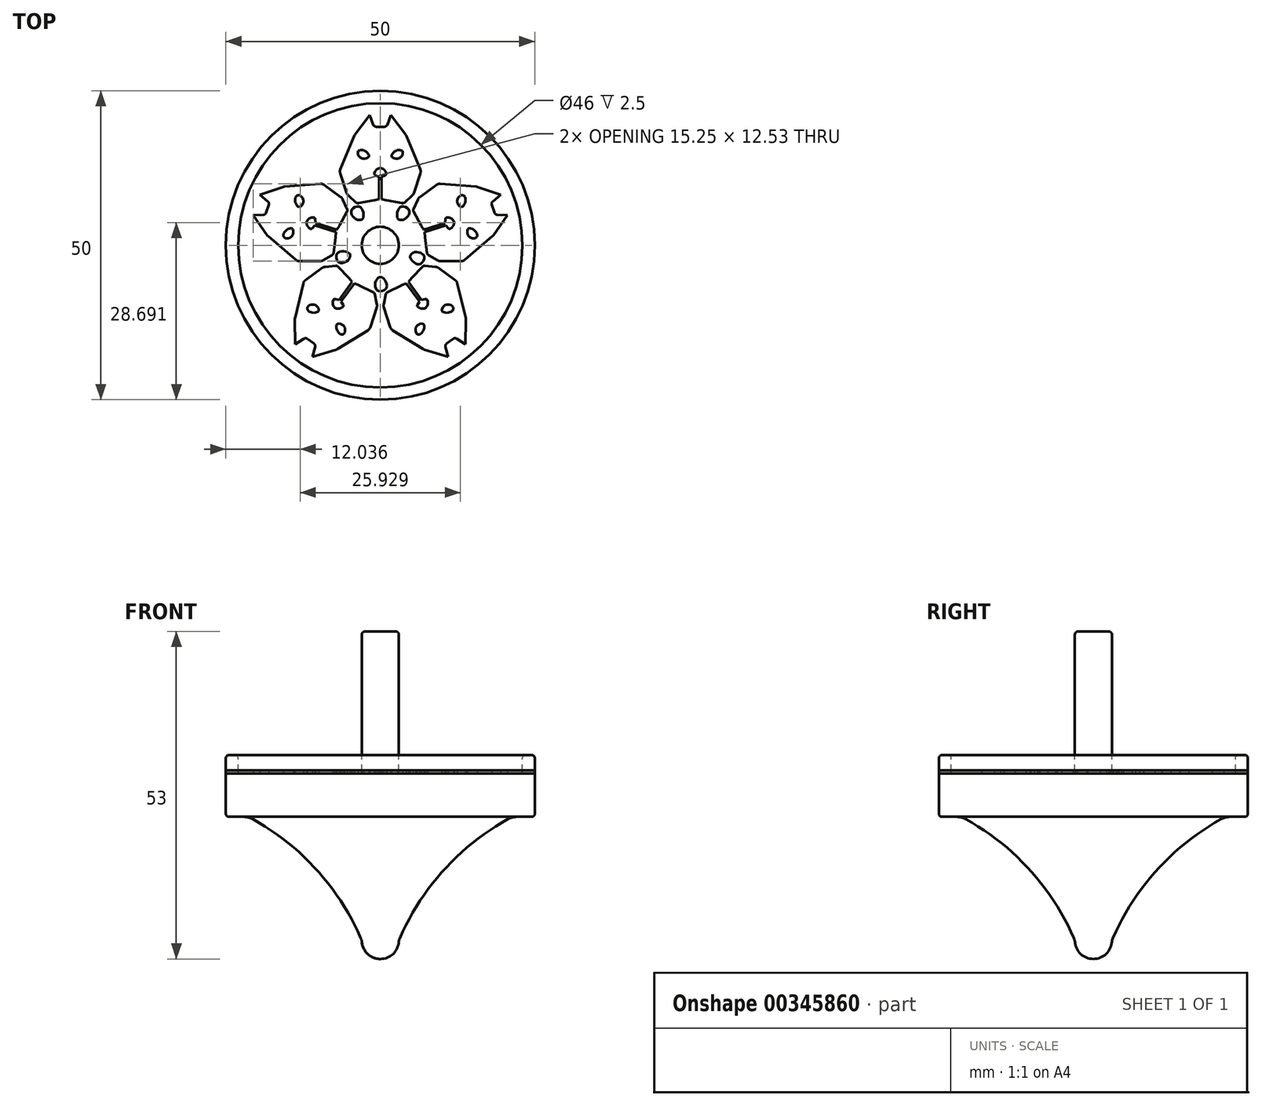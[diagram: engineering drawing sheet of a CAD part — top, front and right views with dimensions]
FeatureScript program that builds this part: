
annotation { "Feature Type Name" : "Feature", "Feature Type Description" : "" }
export const myFeature = defineFeature(function(context is Context, id is Id, definition is map)
    precondition{}
    {
        {
            var Q0;
            Q0=qCreatedBy(makeId("Front.planeOp"),FACE);
            var sketch = newSketch(context, id + "F0", { "sketchPlane" : qUnion([Q0])});
            skLineSegment(sketch, "E0", {"start": v(0, 20) * mm, "end": v(2.5, 20) * mm});
            skLineSegment(sketch, "E1.0", {"start": v(22.12, -10) * mm, "end": v(24.5, -10) * mm});
            skLineSegment(sketch, "E2.0", {"start": v(3, -3) * mm, "end": v(3, 19.5) * mm});
            skLineSegment(sketch, "E3", {"start": v(3, -30) * mm, "end": v(3, -30) * mm});
            skLineSegment(sketch, "E4", {"start": v(0, -33) * mm, "end": v(0, -33) * mm});
            skPoint(sketch, "E5.visualSharp", {"position": v(3, -33) * mm});
            skArc(sketch, "E6", {"start": v(20.66, -10.38) * mm, "mid": v(10.32, -18.56) * mm, "end": v(3.15, -29.64) * mm});
            skPoint(sketch, "E7.visualSharp", {"position": v(3, 20) * mm});
            skArc(sketch, "E7.filletArc", {"start": v(3, 19.5) * mm, "mid": v(2.85, 19.85) * mm, "end": v(2.5, 20) * mm});
            skPoint(sketch, "E8.visualSharp", {"position": v(25, 0) * mm});
            skPoint(sketch, "E9.visualSharp", {"position": v(25, -10) * mm});
            skArc(sketch, "E9.filletArc", {"start": v(24.5, -10) * mm, "mid": v(24.85, -9.85) * mm, "end": v(25, -9.5) * mm});
            skArc(sketch, "E10.filletArc", {"start": v(22.12, -10) * mm, "mid": v(21.37, -10.1) * mm, "end": v(20.66, -10.38) * mm});
            skPoint(sketch, "E11.orphan", {"position": v(0, 0) * mm});
            skPoint(sketch, "E12.visualSharp", {"position": v(3, -30) * mm});
            skArc(sketch, "E13.filletArc", {"start": v(0, -33) * mm, "mid": v(2.06, -32.18) * mm, "end": v(3, -30.16) * mm});
            skLineSegment(sketch, "E14", {"start": v(3.08, -29.83) * mm, "end": v(3.15, -29.64) * mm});
            skArc(sketch, "E15.filletArc", {"start": v(3.08, -29.83) * mm, "mid": v(3.02, -30) * mm, "end": v(3, -30.16) * mm});
            skLineSegment(sketch, "E16", {"start": v(0, 20) * mm, "end": v(0, -33) * mm});
            skLineSegment(sketch, "E17.0", {"start": v(3, -3) * mm, "end": v(23, -3) * mm});
            skPoint(sketch, "E18.visualSharp", {"position": v(23, 0) * mm});
            skPoint(sketch, "E19.orphan", {"position": v(23, -10) * mm});
            skLineSegment(sketch, "E20", {"start": v(23, -3) * mm, "end": v(25, -3) * mm});
            skLineSegment(sketch, "E21", {"start": v(25, -3) * mm, "end": v(25, -9.5) * mm});
            skSolve(sketch);
        }
        {
            var Q0;
            Q0 = qSketchRegion(id + "F0", true);
            var Q1;
            Q1=sQuery(id+"F0.wireOp",EDGE,"E16");
            revolve(context, id + "F1", {"entities" : qUnion([Q0]), "axis" : qUnion([Q1]), "revolveType" : RevolveType.FULL});
        }
        {
            var Q0;
            Q0=qCreatedBy(makeId("Front.planeOp"),FACE);
            var sketch = newSketch(context, id + "F2", { "sketchPlane" : qUnion([Q0])});
            skLineSegment(sketch, "E22", {"start": v(0, 17.36) * mm, "end": v(0, 0) * mm});
            skLineSegment(sketch, "E23", {"start": v(23.5, 0) * mm, "end": v(24.5, 0) * mm});
            skLineSegment(sketch, "E24", {"start": v(23, -0.5) * mm, "end": v(23, -3) * mm});
            skLineSegment(sketch, "E25.0", {"start": v(25, -0.5) * mm, "end": v(25, -3) * mm});
            skPoint(sketch, "E26.visualSharp", {"position": v(23, 0) * mm});
            skArc(sketch, "E26.filletArc", {"start": v(23.5, 0) * mm, "mid": v(23.15, -0.15) * mm, "end": v(23, -0.5) * mm});
            skPoint(sketch, "E27.visualSharp", {"position": v(25, 0) * mm});
            skArc(sketch, "E27.filletArc", {"start": v(25, -0.5) * mm, "mid": v(24.85, -0.15) * mm, "end": v(24.5, 0) * mm});
            skLineSegment(sketch, "E28", {"start": v(23, -3) * mm, "end": v(25, -3) * mm});
            skSolve(sketch);
        }
        {
            var Q0;
            Q0=makeQuery(id+"F2.imprint","IMPRINT",FACE,{"disambiguationData":[TD([[makeQuery(id+"F2.imprint","IMPRINT",EDGE,{"derivedFrom":sQuery(id+"F2.wireOp",EDGE,"E23")}),-1.0]])]});
            var Q1;
            Q1=sQuery(id+"F2.wireOp",EDGE,"E22");
            revolve(context, id + "F3", {"entities" : qUnion([Q0]), "axis" : qUnion([Q1]), "revolveType" : RevolveType.FULL});
        }
        {
            var Q0;
            Q0=makeQuery(id+"F1.opRevolve","SWEPT_FACE",FACE,{"disambiguationData":[OSD([sQuery(id+"F0.wireOp",EDGE,"E17.0"),sQuery(id+"F0.wireOp",EDGE,"E20")])]});
            var sketch = newSketch(context, id + "F4", { "sketchPlane" : qUnion([Q0])});
            skLineSegment(sketch, "E29", {"start": v(0.2, 7.45) * mm, "end": v(0.97, 7.28) * mm});
            skLineSegment(sketch, "E30", {"start": v(1.02, 7.27) * mm, "end": v(3.5, 6.81) * mm});
            skLineSegment(sketch, "E31", {"start": v(3.92, 6.93) * mm, "end": v(5.17, 8.06) * mm});
            skLineSegment(sketch, "E32", {"start": v(5.45, 8.5) * mm, "end": v(6.48, 11.63) * mm});
            skLineSegment(sketch, "E33", {"start": v(6.46, 12.33) * mm, "end": v(4.25, 17.65) * mm});
            skLineSegment(sketch, "E34", {"start": v(4.13, 17.86) * mm, "end": v(1.75, 21.08) * mm});
            skLineSegment(sketch, "E35", {"start": v(1.75, 21.08) * mm, "end": v(1.13, 19.5) * mm});
            skLineSegment(sketch, "E36", {"start": v(0.67, 19.19) * mm, "end": v(0, 19.19) * mm});
            skPoint(sketch, "E37.visualSharp", {"position": v(1, 7.27) * mm});
            skArc(sketch, "E37.filletArc", {"start": v(0.97, 7.28) * mm, "mid": v(1, 7.27) * mm, "end": v(1.02, 7.27) * mm});
            skPoint(sketch, "E38.visualSharp", {"position": v(3.74, 6.77) * mm});
            skArc(sketch, "E38.filletArc", {"start": v(3.5, 6.81) * mm, "mid": v(3.72, 6.82) * mm, "end": v(3.92, 6.93) * mm});
            skPoint(sketch, "E39.visualSharp", {"position": v(5.37, 8.24) * mm});
            skArc(sketch, "E39.filletArc", {"start": v(5.17, 8.06) * mm, "mid": v(5.34, 8.26) * mm, "end": v(5.45, 8.5) * mm});
            skPoint(sketch, "E40.visualSharp", {"position": v(6.6, 11.99) * mm});
            skArc(sketch, "E40.filletArc", {"start": v(6.48, 11.63) * mm, "mid": v(6.53, 11.98) * mm, "end": v(6.46, 12.33) * mm});
            skPoint(sketch, "E41.visualSharp", {"position": v(4.2, 17.76) * mm});
            skArc(sketch, "E41.filletArc", {"start": v(4.25, 17.65) * mm, "mid": v(4.2, 17.76) * mm, "end": v(4.13, 17.86) * mm});
            skPoint(sketch, "E42.visualSharp", {"position": v(1, 19.19) * mm});
            skArc(sketch, "E42.filletArc", {"start": v(0.67, 19.19) * mm, "mid": v(0.95, 19.27) * mm, "end": v(1.13, 19.5) * mm});
            skLineSegment(sketch, "E43", {"start": v(0.2, 11.08) * mm, "end": v(0.76, 11.3) * mm});
            skLineSegment(sketch, "E44", {"start": v(0.93, 11.7) * mm, "end": v(0.86, 11.88) * mm});
            skLineSegment(sketch, "E45", {"start": v(0.24, 12.46) * mm, "end": v(0, 12.54) * mm});
            skFitSpline(sketch, "E46", {"points": [v(1.85, 14.44) * mm, v(2.8, 15.4) * mm, v(3.63, 15.1) * mm, v(2.98, 14.05) * mm, v(1.85, 14.44) * mm]});
            skPoint(sketch, "E47.1.internal.snap0", {"position": v(0.49, 7.39) * mm});
            skPoint(sketch, "E48.visualSharp", {"position": v(0.68, 12.31) * mm});
            skArc(sketch, "E48.filletArc", {"start": v(0.86, 11.88) * mm, "mid": v(0.61, 12.24) * mm, "end": v(0.24, 12.46) * mm});
            skPoint(sketch, "E49.visualSharp", {"position": v(1.04, 11.41) * mm});
            skArc(sketch, "E49.filletArc", {"start": v(0.76, 11.3) * mm, "mid": v(0.93, 11.46) * mm, "end": v(0.93, 11.7) * mm});
            skLineSegment(sketch, "E50.MirrorCS", {"start": v(-0.67, 19.19) * mm, "end": v(0, 19.19) * mm});
            skPoint(sketch, "E51.MirrorP", {"position": v(-1, 19.19) * mm});
            skArc(sketch, "E52.MirrorCS", {"start": v(-0.67, 19.19) * mm, "mid": v(-0.95, 19.27) * mm, "end": v(-1.13, 19.5) * mm});
            skLineSegment(sketch, "E53.MirrorCS", {"start": v(-1.75, 21.08) * mm, "end": v(-1.13, 19.5) * mm});
            skLineSegment(sketch, "E54.MirrorCS", {"start": v(-4.13, 17.86) * mm, "end": v(-1.75, 21.08) * mm});
            skArc(sketch, "E55.MirrorCS", {"start": v(-4.25, 17.65) * mm, "mid": v(-4.2, 17.76) * mm, "end": v(-4.13, 17.86) * mm});
            skLineSegment(sketch, "E56.MirrorCS", {"start": v(-6.46, 12.33) * mm, "end": v(-4.25, 17.65) * mm});
            skArc(sketch, "E57.MirrorCS", {"start": v(-6.48, 11.63) * mm, "mid": v(-6.53, 11.98) * mm, "end": v(-6.46, 12.33) * mm});
            skLineSegment(sketch, "E58.MirrorCS", {"start": v(-5.45, 8.5) * mm, "end": v(-6.48, 11.63) * mm});
            skArc(sketch, "E59.MirrorCS", {"start": v(-5.17, 8.06) * mm, "mid": v(-5.34, 8.26) * mm, "end": v(-5.45, 8.5) * mm});
            skLineSegment(sketch, "E60.MirrorCS", {"start": v(-3.92, 6.93) * mm, "end": v(-5.17, 8.06) * mm});
            skArc(sketch, "E61.MirrorCS", {"start": v(-3.5, 6.81) * mm, "mid": v(-3.72, 6.82) * mm, "end": v(-3.92, 6.93) * mm});
            skLineSegment(sketch, "E62.MirrorCS", {"start": v(-1.02, 7.27) * mm, "end": v(-3.5, 6.81) * mm});
            skLineSegment(sketch, "E63.MirrorCS", {"start": v(-0.2, 7.45) * mm, "end": v(-0.97, 7.28) * mm});
            skLineSegment(sketch, "E64.MirrorCS", {"start": v(-0.24, 12.46) * mm, "end": v(0, 12.54) * mm});
            skArc(sketch, "E65.MirrorCS", {"start": v(-0.86, 11.88) * mm, "mid": v(-0.61, 12.24) * mm, "end": v(-0.24, 12.46) * mm});
            skLineSegment(sketch, "E66.MirrorCS", {"start": v(-0.93, 11.7) * mm, "end": v(-0.86, 11.88) * mm});
            skArc(sketch, "E67.MirrorCS", {"start": v(-0.76, 11.3) * mm, "mid": v(-0.93, 11.46) * mm, "end": v(-0.93, 11.7) * mm});
            skLineSegment(sketch, "E68.MirrorCS", {"start": v(-0.2, 11.08) * mm, "end": v(-0.76, 11.3) * mm});
            skFitSpline(sketch, "E69.MirrorC", {"points": [v(-1.85, 14.44) * mm, v(-2.8, 15.4) * mm, v(-3.63, 15.1) * mm, v(-2.98, 14.05) * mm, v(-1.85, 14.44) * mm]});
            skFitSpline(sketch, "E70", {"points": [v(2.97, 4.18) * mm, v(2.7, 4.91) * mm, v(3.34, 6.21) * mm, v(4.7, 5.63) * mm, v(3.98, 4.26) * mm, v(2.97, 4.18) * mm]});
            skPoint(sketch, "E71.MirrorP", {"position": v(-4.2, 17.76) * mm});
            skPoint(sketch, "E72.MirrorP", {"position": v(-6.6, 11.99) * mm});
            skPoint(sketch, "E73.MirrorP", {"position": v(-5.37, 8.24) * mm});
            skPoint(sketch, "E74.MirrorP", {"position": v(-3.74, 6.77) * mm});
            skPoint(sketch, "E75.MirrorP", {"position": v(-0.49, 7.39) * mm});
            skPoint(sketch, "E76.MirrorP", {"position": v(-1, 7.27) * mm});
            skPoint(sketch, "E77.MirrorP", {"position": v(-0.68, 12.31) * mm});
            skPoint(sketch, "E78.MirrorP", {"position": v(-1.04, 11.41) * mm});
            skArc(sketch, "E79.MirrorCS", {"start": v(-0.97, 7.28) * mm, "mid": v(-1, 7.27) * mm, "end": v(-1.02, 7.27) * mm});
            skLineSegment(sketch, "E80.0", {"start": v(-0.2, 11.08) * mm, "end": v(-0.2, 7.45) * mm});
            skLineSegment(sketch, "E81.0", {"start": v(0.2, 11.08) * mm, "end": v(0.2, 7.45) * mm});
            skLineSegment(sketch, "E82", {"start": v(0, 7.5) * mm, "end": v(0, 0) * mm});
            skLineSegment(sketch, "E83.1.0", {"start": v(-18.26, 1.6) * mm, "end": v(-20.59, 4.85) * mm});
            skLineSegment(sketch, "E83.1.1", {"start": v(-20.59, 4.85) * mm, "end": v(-18.9, 4.95) * mm});
            skArc(sketch, "E83.1.2", {"start": v(-18.45, 5.3) * mm, "mid": v(-18.62, 5.05) * mm, "end": v(-18.9, 4.95) * mm});
            skLineSegment(sketch, "E83.1.3", {"start": v(-18.45, 5.3) * mm, "end": v(-18.25, 5.93) * mm});
            skLineSegment(sketch, "E83.1.4", {"start": v(-18.04, 6.56) * mm, "end": v(-18.25, 5.93) * mm});
            skArc(sketch, "E83.1.5", {"start": v(-18.04, 6.56) * mm, "mid": v(-18.04, 6.86) * mm, "end": v(-18.2, 7.1) * mm});
            skLineSegment(sketch, "E83.1.6", {"start": v(-19.5, 8.17) * mm, "end": v(-18.2, 7.1) * mm});
            skLineSegment(sketch, "E83.1.7", {"start": v(-15.71, 9.45) * mm, "end": v(-19.5, 8.17) * mm});
            skArc(sketch, "E83.1.8", {"start": v(-15.47, 9.5) * mm, "mid": v(-15.6, 9.48) * mm, "end": v(-15.71, 9.45) * mm});
            skLineSegment(sketch, "E83.1.9", {"start": v(-9.73, 9.95) * mm, "end": v(-15.47, 9.5) * mm});
            skArc(sketch, "E83.1.10", {"start": v(-9.06, 9.76) * mm, "mid": v(-9.38, 9.92) * mm, "end": v(-9.73, 9.95) * mm});
            skLineSegment(sketch, "E83.1.11", {"start": v(-6.39, 7.81) * mm, "end": v(-9.06, 9.76) * mm});
            skArc(sketch, "E83.1.12", {"start": v(-6.07, 7.4) * mm, "mid": v(-6.2, 7.63) * mm, "end": v(-6.39, 7.81) * mm});
            skLineSegment(sketch, "E83.1.13", {"start": v(-5.38, 5.87) * mm, "end": v(-6.07, 7.4) * mm});
            skArc(sketch, "E83.1.14", {"start": v(-5.4, 5.43) * mm, "mid": v(-5.34, 5.65) * mm, "end": v(-5.38, 5.87) * mm});
            skLineSegment(sketch, "E83.1.15", {"start": v(-6.6, 3.21) * mm, "end": v(-5.4, 5.43) * mm});
            skLineSegment(sketch, "E83.1.16", {"start": v(-7.03, 2.5) * mm, "end": v(-6.62, 3.17) * mm});
            skLineSegment(sketch, "E83.1.17", {"start": v(-7.15, 2.11) * mm, "end": v(-7.22, 1.32) * mm});
            skLineSegment(sketch, "E83.1.18", {"start": v(-7.23, 1.28) * mm, "end": v(-7.56, -1.22) * mm});
            skArc(sketch, "E83.1.19", {"start": v(-7.56, -1.22) * mm, "mid": v(-7.64, -1.43) * mm, "end": v(-7.8, -1.58) * mm});
            skLineSegment(sketch, "E83.1.20", {"start": v(-7.8, -1.58) * mm, "end": v(-9.26, -2.43) * mm});
            skArc(sketch, "E83.1.21", {"start": v(-9.26, -2.43) * mm, "mid": v(-9.5, -2.53) * mm, "end": v(-9.76, -2.56) * mm});
            skLineSegment(sketch, "E83.1.22", {"start": v(-9.76, -2.56) * mm, "end": v(-13.07, -2.57) * mm});
            skArc(sketch, "E83.1.23", {"start": v(-13.07, -2.57) * mm, "mid": v(-13.42, -2.51) * mm, "end": v(-13.72, -2.33) * mm});
            skLineSegment(sketch, "E83.1.24", {"start": v(-13.72, -2.33) * mm, "end": v(-18.1, 1.41) * mm});
            skArc(sketch, "E83.1.25", {"start": v(-18.1, 1.41) * mm, "mid": v(-18.19, 1.5) * mm, "end": v(-18.26, 1.6) * mm});
            skLineSegment(sketch, "E83.2.0", {"start": v(-7.16, -16.88) * mm, "end": v(-10.98, -18.08) * mm});
            skLineSegment(sketch, "E83.2.1", {"start": v(-10.98, -18.08) * mm, "end": v(-10.55, -16.45) * mm});
            skArc(sketch, "E83.2.2", {"start": v(-10.74, -15.91) * mm, "mid": v(-10.56, -16.15) * mm, "end": v(-10.55, -16.45) * mm});
            skLineSegment(sketch, "E83.2.3", {"start": v(-10.74, -15.91) * mm, "end": v(-11.28, -15.52) * mm});
            skLineSegment(sketch, "E83.2.4", {"start": v(-11.82, -15.13) * mm, "end": v(-11.28, -15.52) * mm});
            skArc(sketch, "E83.2.5", {"start": v(-11.82, -15.13) * mm, "mid": v(-12.1, -15.04) * mm, "end": v(-12.38, -15.11) * mm});
            skLineSegment(sketch, "E83.2.6", {"start": v(-13.8, -16.03) * mm, "end": v(-12.38, -15.11) * mm});
            skLineSegment(sketch, "E83.2.7", {"start": v(-13.84, -12.02) * mm, "end": v(-13.8, -16.03) * mm});
            skArc(sketch, "E83.2.8", {"start": v(-13.81, -11.78) * mm, "mid": v(-13.83, -11.9) * mm, "end": v(-13.84, -12.02) * mm});
            skLineSegment(sketch, "E83.2.9", {"start": v(-12.47, -6.18) * mm, "end": v(-13.81, -11.78) * mm});
            skArc(sketch, "E83.2.10", {"start": v(-12.08, -5.6) * mm, "mid": v(-12.33, -5.85) * mm, "end": v(-12.47, -6.18) * mm});
            skLineSegment(sketch, "E83.2.11", {"start": v(-9.4, -3.66) * mm, "end": v(-12.08, -5.6) * mm});
            skArc(sketch, "E83.2.12", {"start": v(-8.92, -3.48) * mm, "mid": v(-9.17, -3.54) * mm, "end": v(-9.4, -3.66) * mm});
            skLineSegment(sketch, "E83.2.13", {"start": v(-7.25, -3.3) * mm, "end": v(-8.92, -3.48) * mm});
            skArc(sketch, "E83.2.14", {"start": v(-6.83, -3.46) * mm, "mid": v(-7.02, -3.33) * mm, "end": v(-7.25, -3.3) * mm});
            skLineSegment(sketch, "E83.2.15", {"start": v(-5.1, -5.28) * mm, "end": v(-6.83, -3.46) * mm});
            skLineSegment(sketch, "E83.2.16", {"start": v(-4.54, -5.91) * mm, "end": v(-5.06, -5.31) * mm});
            skLineSegment(sketch, "E83.2.17", {"start": v(-4.22, -6.15) * mm, "end": v(-3.49, -6.46) * mm});
            skLineSegment(sketch, "E83.2.18", {"start": v(-3.45, -6.48) * mm, "end": v(-1.18, -7.57) * mm});
            skArc(sketch, "E83.2.19", {"start": v(-1.18, -7.57) * mm, "mid": v(-1, -7.7) * mm, "end": v(-0.9, -7.91) * mm});
            skLineSegment(sketch, "E83.2.20", {"start": v(-0.9, -7.91) * mm, "end": v(-0.55, -9.56) * mm});
            skArc(sketch, "E83.2.21", {"start": v(-0.55, -9.56) * mm, "mid": v(-0.53, -9.82) * mm, "end": v(-0.58, -10.08) * mm});
            skLineSegment(sketch, "E83.2.22", {"start": v(-0.58, -10.08) * mm, "end": v(-1.6, -13.22) * mm});
            skArc(sketch, "E83.2.23", {"start": v(-1.6, -13.22) * mm, "mid": v(-1.76, -13.53) * mm, "end": v(-2.02, -13.77) * mm});
            skLineSegment(sketch, "E83.2.24", {"start": v(-2.02, -13.77) * mm, "end": v(-6.94, -16.78) * mm});
            skArc(sketch, "E83.2.25", {"start": v(-6.94, -16.78) * mm, "mid": v(-7.04, -16.83) * mm, "end": v(-7.16, -16.88) * mm});
            skLineSegment(sketch, "E83.3.0", {"start": v(13.84, -12.02) * mm, "end": v(13.8, -16.03) * mm});
            skLineSegment(sketch, "E83.3.1", {"start": v(13.8, -16.03) * mm, "end": v(12.38, -15.11) * mm});
            skArc(sketch, "E83.3.2", {"start": v(11.82, -15.13) * mm, "mid": v(12.1, -15.04) * mm, "end": v(12.38, -15.11) * mm});
            skLineSegment(sketch, "E83.3.3", {"start": v(11.82, -15.13) * mm, "end": v(11.28, -15.52) * mm});
            skLineSegment(sketch, "E83.3.4", {"start": v(10.74, -15.91) * mm, "end": v(11.28, -15.52) * mm});
            skArc(sketch, "E83.3.5", {"start": v(10.74, -15.91) * mm, "mid": v(10.56, -16.15) * mm, "end": v(10.55, -16.45) * mm});
            skLineSegment(sketch, "E83.3.6", {"start": v(10.98, -18.08) * mm, "end": v(10.55, -16.45) * mm});
            skLineSegment(sketch, "E83.3.7", {"start": v(7.16, -16.88) * mm, "end": v(10.98, -18.08) * mm});
            skArc(sketch, "E83.3.8", {"start": v(6.94, -16.78) * mm, "mid": v(7.04, -16.83) * mm, "end": v(7.16, -16.88) * mm});
            skLineSegment(sketch, "E83.3.9", {"start": v(2.02, -13.77) * mm, "end": v(6.94, -16.78) * mm});
            skArc(sketch, "E83.3.10", {"start": v(1.6, -13.22) * mm, "mid": v(1.76, -13.53) * mm, "end": v(2.02, -13.77) * mm});
            skLineSegment(sketch, "E83.3.11", {"start": v(0.58, -10.08) * mm, "end": v(1.6, -13.22) * mm});
            skArc(sketch, "E83.3.12", {"start": v(0.55, -9.56) * mm, "mid": v(0.53, -9.82) * mm, "end": v(0.58, -10.08) * mm});
            skLineSegment(sketch, "E83.3.13", {"start": v(0.9, -7.91) * mm, "end": v(0.55, -9.56) * mm});
            skArc(sketch, "E83.3.14", {"start": v(1.18, -7.57) * mm, "mid": v(1, -7.7) * mm, "end": v(0.9, -7.91) * mm});
            skLineSegment(sketch, "E83.3.15", {"start": v(3.45, -6.48) * mm, "end": v(1.18, -7.57) * mm});
            skLineSegment(sketch, "E83.3.16", {"start": v(4.22, -6.15) * mm, "end": v(3.49, -6.46) * mm});
            skLineSegment(sketch, "E83.3.17", {"start": v(4.54, -5.91) * mm, "end": v(5.06, -5.31) * mm});
            skLineSegment(sketch, "E83.3.18", {"start": v(5.1, -5.28) * mm, "end": v(6.83, -3.46) * mm});
            skArc(sketch, "E83.3.19", {"start": v(6.83, -3.46) * mm, "mid": v(7.02, -3.33) * mm, "end": v(7.25, -3.3) * mm});
            skLineSegment(sketch, "E83.3.20", {"start": v(7.25, -3.3) * mm, "end": v(8.92, -3.48) * mm});
            skArc(sketch, "E83.3.21", {"start": v(8.92, -3.48) * mm, "mid": v(9.17, -3.54) * mm, "end": v(9.4, -3.66) * mm});
            skLineSegment(sketch, "E83.3.22", {"start": v(9.4, -3.66) * mm, "end": v(12.08, -5.6) * mm});
            skArc(sketch, "E83.3.23", {"start": v(12.08, -5.6) * mm, "mid": v(12.33, -5.85) * mm, "end": v(12.47, -6.18) * mm});
            skLineSegment(sketch, "E83.3.24", {"start": v(12.47, -6.18) * mm, "end": v(13.81, -11.78) * mm});
            skArc(sketch, "E83.3.25", {"start": v(13.81, -11.78) * mm, "mid": v(13.83, -11.9) * mm, "end": v(13.84, -12.02) * mm});
            skLineSegment(sketch, "E83.4.0", {"start": v(15.71, 9.45) * mm, "end": v(19.5, 8.17) * mm});
            skLineSegment(sketch, "E83.4.1", {"start": v(19.5, 8.17) * mm, "end": v(18.2, 7.1) * mm});
            skArc(sketch, "E83.4.2", {"start": v(18.04, 6.56) * mm, "mid": v(18.04, 6.86) * mm, "end": v(18.2, 7.1) * mm});
            skLineSegment(sketch, "E83.4.3", {"start": v(18.04, 6.56) * mm, "end": v(18.25, 5.93) * mm});
            skLineSegment(sketch, "E83.4.4", {"start": v(18.45, 5.3) * mm, "end": v(18.25, 5.93) * mm});
            skArc(sketch, "E83.4.5", {"start": v(18.45, 5.3) * mm, "mid": v(18.62, 5.05) * mm, "end": v(18.9, 4.95) * mm});
            skLineSegment(sketch, "E83.4.6", {"start": v(20.59, 4.85) * mm, "end": v(18.9, 4.95) * mm});
            skLineSegment(sketch, "E83.4.7", {"start": v(18.26, 1.6) * mm, "end": v(20.59, 4.85) * mm});
            skArc(sketch, "E83.4.8", {"start": v(18.1, 1.41) * mm, "mid": v(18.19, 1.5) * mm, "end": v(18.26, 1.6) * mm});
            skLineSegment(sketch, "E83.4.9", {"start": v(13.72, -2.33) * mm, "end": v(18.1, 1.41) * mm});
            skArc(sketch, "E83.4.10", {"start": v(13.07, -2.57) * mm, "mid": v(13.42, -2.51) * mm, "end": v(13.72, -2.33) * mm});
            skLineSegment(sketch, "E83.4.11", {"start": v(9.76, -2.56) * mm, "end": v(13.07, -2.57) * mm});
            skArc(sketch, "E83.4.12", {"start": v(9.26, -2.43) * mm, "mid": v(9.5, -2.53) * mm, "end": v(9.76, -2.56) * mm});
            skLineSegment(sketch, "E83.4.13", {"start": v(7.8, -1.58) * mm, "end": v(9.26, -2.43) * mm});
            skArc(sketch, "E83.4.14", {"start": v(7.56, -1.22) * mm, "mid": v(7.64, -1.43) * mm, "end": v(7.8, -1.58) * mm});
            skLineSegment(sketch, "E83.4.15", {"start": v(7.23, 1.28) * mm, "end": v(7.56, -1.22) * mm});
            skLineSegment(sketch, "E83.4.16", {"start": v(7.15, 2.11) * mm, "end": v(7.22, 1.32) * mm});
            skLineSegment(sketch, "E83.4.17", {"start": v(7.03, 2.5) * mm, "end": v(6.62, 3.17) * mm});
            skLineSegment(sketch, "E83.4.18", {"start": v(6.6, 3.21) * mm, "end": v(5.4, 5.43) * mm});
            skArc(sketch, "E83.4.19", {"start": v(5.4, 5.43) * mm, "mid": v(5.34, 5.65) * mm, "end": v(5.38, 5.87) * mm});
            skLineSegment(sketch, "E83.4.20", {"start": v(5.38, 5.87) * mm, "end": v(6.07, 7.4) * mm});
            skArc(sketch, "E83.4.21", {"start": v(6.07, 7.4) * mm, "mid": v(6.2, 7.63) * mm, "end": v(6.39, 7.81) * mm});
            skLineSegment(sketch, "E83.4.22", {"start": v(6.39, 7.81) * mm, "end": v(9.06, 9.76) * mm});
            skArc(sketch, "E83.4.23", {"start": v(9.06, 9.76) * mm, "mid": v(9.38, 9.92) * mm, "end": v(9.73, 9.95) * mm});
            skLineSegment(sketch, "E83.4.24", {"start": v(9.73, 9.95) * mm, "end": v(15.47, 9.5) * mm});
            skArc(sketch, "E83.4.25", {"start": v(15.47, 9.5) * mm, "mid": v(15.6, 9.48) * mm, "end": v(15.71, 9.45) * mm});
            skPoint(sketch, "E83.center", {"position": v(0, 0) * mm});
            skArc(sketch, "E84.1.0", {"start": v(-5.81, -4.48) * mm, "mid": v(-5.8, -4.5) * mm, "end": v(-5.78, -4.51) * mm});
            skArc(sketch, "E84.2.0", {"start": v(6.79, -2.8) * mm, "mid": v(6.8, -2.77) * mm, "end": v(6.8, -2.75) * mm});
            skArc(sketch, "E85.1.0", {"start": v(-7.22, 1.32) * mm, "mid": v(-7.22, 1.3) * mm, "end": v(-7.23, 1.28) * mm});
            skArc(sketch, "E85.2.0", {"start": v(-3.49, -6.46) * mm, "mid": v(-3.47, -6.47) * mm, "end": v(-3.45, -6.48) * mm});
            skArc(sketch, "E85.3.0", {"start": v(5.06, -5.31) * mm, "mid": v(5.08, -5.3) * mm, "end": v(5.1, -5.28) * mm});
            skArc(sketch, "E85.4.0", {"start": v(6.62, 3.17) * mm, "mid": v(6.6, 3.2) * mm, "end": v(6.6, 3.21) * mm});
            skArc(sketch, "E86.1.0", {"start": v(-6.62, 3.17) * mm, "mid": v(-6.6, 3.2) * mm, "end": v(-6.6, 3.21) * mm});
            skArc(sketch, "E86.2.0", {"start": v(-5.06, -5.31) * mm, "mid": v(-5.08, -5.3) * mm, "end": v(-5.1, -5.28) * mm});
            skArc(sketch, "E86.3.0", {"start": v(3.49, -6.46) * mm, "mid": v(3.47, -6.47) * mm, "end": v(3.45, -6.48) * mm});
            skArc(sketch, "E86.4.0", {"start": v(7.22, 1.32) * mm, "mid": v(7.22, 1.3) * mm, "end": v(7.23, 1.28) * mm});
            skPoint(sketch, "E87.orphan", {"position": v(0, 7.5) * mm});
            skPoint(sketch, "E88.orphan", {"position": v(0, 11) * mm});
            skArc(sketch, "E89.1.0", {"start": v(-11.56, 2.86) * mm, "mid": v(-11.83, 3.2) * mm, "end": v(-11.92, 3.62) * mm});
            skLineSegment(sketch, "E89.1.1", {"start": v(-11.92, 3.62) * mm, "end": v(-11.92, 3.87) * mm});
            skLineSegment(sketch, "E89.1.2", {"start": v(-11.78, 4.08) * mm, "end": v(-11.92, 3.87) * mm});
            skArc(sketch, "E89.1.3", {"start": v(-11.03, 4.49) * mm, "mid": v(-11.45, 4.36) * mm, "end": v(-11.78, 4.08) * mm});
            skLineSegment(sketch, "E89.1.4", {"start": v(-10.83, 4.5) * mm, "end": v(-11.03, 4.49) * mm});
            skArc(sketch, "E89.1.5", {"start": v(-10.51, 4.22) * mm, "mid": v(-10.62, 4.42) * mm, "end": v(-10.83, 4.5) * mm});
            skLineSegment(sketch, "E89.1.6", {"start": v(-10.48, 3.61) * mm, "end": v(-10.51, 4.22) * mm});
            skLineSegment(sketch, "E89.1.7", {"start": v(-10.6, 3.23) * mm, "end": v(-10.99, 2.77) * mm});
            skArc(sketch, "E89.1.8", {"start": v(-10.99, 2.77) * mm, "mid": v(-11.19, 2.66) * mm, "end": v(-11.4, 2.73) * mm});
            skLineSegment(sketch, "E89.1.9", {"start": v(-11.4, 2.73) * mm, "end": v(-11.56, 2.86) * mm});
            skLineSegment(sketch, "E89.1.10", {"start": v(-10.6, 3.23) * mm, "end": v(-7.15, 2.11) * mm});
            skLineSegment(sketch, "E89.1.11", {"start": v(-10.48, 3.61) * mm, "end": v(-7.03, 2.5) * mm});
            skArc(sketch, "E89.2.0", {"start": v(-6.29, -10.11) * mm, "mid": v(-6.7, -10.26) * mm, "end": v(-7.13, -10.22) * mm});
            skLineSegment(sketch, "E89.2.1", {"start": v(-7.13, -10.22) * mm, "end": v(-7.37, -10.14) * mm});
            skLineSegment(sketch, "E89.2.2", {"start": v(-7.52, -9.94) * mm, "end": v(-7.37, -10.14) * mm});
            skArc(sketch, "E89.2.3", {"start": v(-7.68, -9.1) * mm, "mid": v(-7.69, -9.54) * mm, "end": v(-7.52, -9.94) * mm});
            skLineSegment(sketch, "E89.2.4", {"start": v(-7.63, -8.91) * mm, "end": v(-7.68, -9.1) * mm});
            skArc(sketch, "E89.2.5", {"start": v(-7.26, -8.7) * mm, "mid": v(-7.49, -8.73) * mm, "end": v(-7.63, -8.91) * mm});
            skLineSegment(sketch, "E89.2.6", {"start": v(-6.67, -8.85) * mm, "end": v(-7.26, -8.7) * mm});
            skLineSegment(sketch, "E89.2.7", {"start": v(-6.35, -9.08) * mm, "end": v(-6.03, -9.6) * mm});
            skArc(sketch, "E89.2.8", {"start": v(-6.03, -9.6) * mm, "mid": v(-5.99, -9.82) * mm, "end": v(-6.12, -10) * mm});
            skLineSegment(sketch, "E89.2.9", {"start": v(-6.12, -10) * mm, "end": v(-6.29, -10.11) * mm});
            skLineSegment(sketch, "E89.2.10", {"start": v(-6.35, -9.08) * mm, "end": v(-4.22, -6.15) * mm});
            skLineSegment(sketch, "E89.2.11", {"start": v(-6.67, -8.85) * mm, "end": v(-4.54, -5.91) * mm});
            skArc(sketch, "E89.3.0", {"start": v(7.68, -9.1) * mm, "mid": v(7.69, -9.54) * mm, "end": v(7.52, -9.94) * mm});
            skLineSegment(sketch, "E89.3.1", {"start": v(7.52, -9.94) * mm, "end": v(7.37, -10.14) * mm});
            skLineSegment(sketch, "E89.3.2", {"start": v(7.13, -10.22) * mm, "end": v(7.37, -10.14) * mm});
            skArc(sketch, "E89.3.3", {"start": v(6.29, -10.11) * mm, "mid": v(6.7, -10.26) * mm, "end": v(7.13, -10.22) * mm});
            skLineSegment(sketch, "E89.3.4", {"start": v(6.12, -10) * mm, "end": v(6.29, -10.11) * mm});
            skArc(sketch, "E89.3.5", {"start": v(6.03, -9.6) * mm, "mid": v(5.99, -9.82) * mm, "end": v(6.12, -10) * mm});
            skLineSegment(sketch, "E89.3.6", {"start": v(6.35, -9.08) * mm, "end": v(6.03, -9.6) * mm});
            skLineSegment(sketch, "E89.3.7", {"start": v(6.67, -8.85) * mm, "end": v(7.26, -8.7) * mm});
            skArc(sketch, "E89.3.8", {"start": v(7.26, -8.7) * mm, "mid": v(7.49, -8.73) * mm, "end": v(7.63, -8.91) * mm});
            skLineSegment(sketch, "E89.3.9", {"start": v(7.63, -8.91) * mm, "end": v(7.68, -9.1) * mm});
            skLineSegment(sketch, "E89.3.10", {"start": v(6.67, -8.85) * mm, "end": v(4.54, -5.91) * mm});
            skLineSegment(sketch, "E89.3.11", {"start": v(6.35, -9.08) * mm, "end": v(4.22, -6.15) * mm});
            skArc(sketch, "E89.4.0", {"start": v(11.03, 4.49) * mm, "mid": v(11.45, 4.36) * mm, "end": v(11.78, 4.08) * mm});
            skLineSegment(sketch, "E89.4.1", {"start": v(11.78, 4.08) * mm, "end": v(11.92, 3.87) * mm});
            skLineSegment(sketch, "E89.4.2", {"start": v(11.92, 3.62) * mm, "end": v(11.92, 3.87) * mm});
            skArc(sketch, "E89.4.3", {"start": v(11.56, 2.86) * mm, "mid": v(11.83, 3.2) * mm, "end": v(11.92, 3.62) * mm});
            skLineSegment(sketch, "E89.4.4", {"start": v(11.4, 2.73) * mm, "end": v(11.56, 2.86) * mm});
            skArc(sketch, "E89.4.5", {"start": v(10.99, 2.77) * mm, "mid": v(11.19, 2.66) * mm, "end": v(11.4, 2.73) * mm});
            skLineSegment(sketch, "E89.4.6", {"start": v(10.6, 3.23) * mm, "end": v(10.99, 2.77) * mm});
            skLineSegment(sketch, "E89.4.7", {"start": v(10.48, 3.61) * mm, "end": v(10.51, 4.22) * mm});
            skArc(sketch, "E89.4.8", {"start": v(10.51, 4.22) * mm, "mid": v(10.62, 4.42) * mm, "end": v(10.83, 4.5) * mm});
            skLineSegment(sketch, "E89.4.9", {"start": v(10.83, 4.5) * mm, "end": v(11.03, 4.49) * mm});
            skLineSegment(sketch, "E89.4.10", {"start": v(10.48, 3.61) * mm, "end": v(7.03, 2.5) * mm});
            skLineSegment(sketch, "E89.4.11", {"start": v(10.6, 3.23) * mm, "end": v(7.15, 2.11) * mm});
            skPoint(sketch, "E90.orphan", {"position": v(-7.13, 2.32) * mm});
            skPoint(sketch, "E91.orphan", {"position": v(-4.4, -6.07) * mm});
            skPoint(sketch, "E92.orphan", {"position": v(4.4, -6.07) * mm});
            skPoint(sketch, "E93.orphan", {"position": v(7.13, 2.32) * mm});
            skFitSpline(sketch, "E94.MirrorC", {"points": [v(-2.97, 4.18) * mm, v(-2.7, 4.91) * mm, v(-3.34, 6.21) * mm, v(-4.7, 5.63) * mm, v(-3.98, 4.26) * mm, v(-2.97, 4.18) * mm]});
            skLineSegment(sketch, "E95", {"start": v(0, 0) * mm, "end": v(7.13, 2.32) * mm});
            skLineSegment(sketch, "E96", {"start": v(0, 0) * mm, "end": v(4.4, -6.07) * mm});
            skLineSegment(sketch, "E97", {"start": v(0, 0) * mm, "end": v(-4.4, -6.07) * mm});
            skLineSegment(sketch, "E98", {"start": v(0, 0) * mm, "end": v(-7.13, 2.32) * mm});
            skFitSpline(sketch, "E99.MirrorC", {"points": [v(4.86, -1.64) * mm, v(5.08, -2.38) * mm, v(6.35, -3.07) * mm, v(7.1, -1.8) * mm, v(5.73, -1.1) * mm, v(4.86, -1.64) * mm]});
            skFitSpline(sketch, "E100.MirrorC", {"points": [v(0.06, -5.13) * mm, v(0.7, -5.56) * mm, v(0.95, -6.99) * mm, v(-0.49, -7.31) * mm, v(-0.72, -5.79) * mm, v(0.06, -5.13) * mm]});
            skFitSpline(sketch, "E101.MirrorC", {"points": [v(-4.9, -1.53) * mm, v(-5.5, -1.06) * mm, v(-6.94, -1.25) * mm, v(-6.8, -2.72) * mm, v(-5.28, -2.47) * mm, v(-4.9, -1.53) * mm]});
            skSolve(sketch);
        }
        {
            var Q0;
            Q0=makeQuery(id+"F4.imprint","IMPRINT",FACE,{"disambiguationData":[TD([[makeQuery(id+"F4.imprint","IMPRINT",EDGE,{"derivedFrom":sQuery(id+"F4.wireOp",EDGE,"E29")}),-1.0]])]});
            var Q1;
            Q1=makeQuery(id+"F4.imprint","IMPRINT",FACE,{"disambiguationData":[TD([[makeQuery(id+"F4.imprint","IMPRINT",EDGE,{"derivedFrom":sQuery(id+"F4.wireOp",EDGE,"E69.MirrorC")}),1.0]])]});
            var Q2;
            Q2=makeQuery(id+"F4.imprint","IMPRINT",FACE,{"disambiguationData":[TD([[makeQuery(id+"F4.imprint","IMPRINT",EDGE,{"derivedFrom":sQuery(id+"F4.wireOp",EDGE,"E46")}),-1.0]])]});
            extrude(context, id + "F5", {"entities" : qUnion([Q0, Q1, Q2]), "depth" : 0.5 * mm});
        }
        {
            var Q0;
            Q0=makeQuery(id+"F4.imprint","IMPRINT",FACE,{"disambiguationData":[TD([[makeQuery(id+"F4.imprint","IMPRINT",EDGE,{"derivedFrom":sQuery(id+"F4.wireOp",EDGE,"E70")}),-1.0]])]});
            extrude(context, id + "F6", {"entities" : qUnion([Q0]), "operationType" : NewBodyOperationType.REMOVE, "depth" : 0.5 * mm});
        }
        {
            var Q0;
            Q0=makeQuery(id+"F5.opExtrude","SWEPT_BODY",BODY,{"disambiguationData":[OSD([sQuery(id+"F4.wireOp",EDGE,"E69.MirrorC")])]});
            var Q1;
            Q1=makeQuery(id+"F5.opExtrude","SWEPT_BODY",BODY,{"disambiguationData":[OSD([sQuery(id+"F4.wireOp",EDGE,"E46")])]});
            var Q2;
            Q2=sQuery(id+"F0.wireOp",EDGE,"E16");
            circularPattern(context, id + "F7", {"operationType" : NewBodyOperationType.ADD, "entities" : qUnion([Q0, Q1]), "axis" : qUnion([Q2]), "angle" : 360 * degree, "instanceCount" : 5, "equalSpace" : true});
        }
    });
